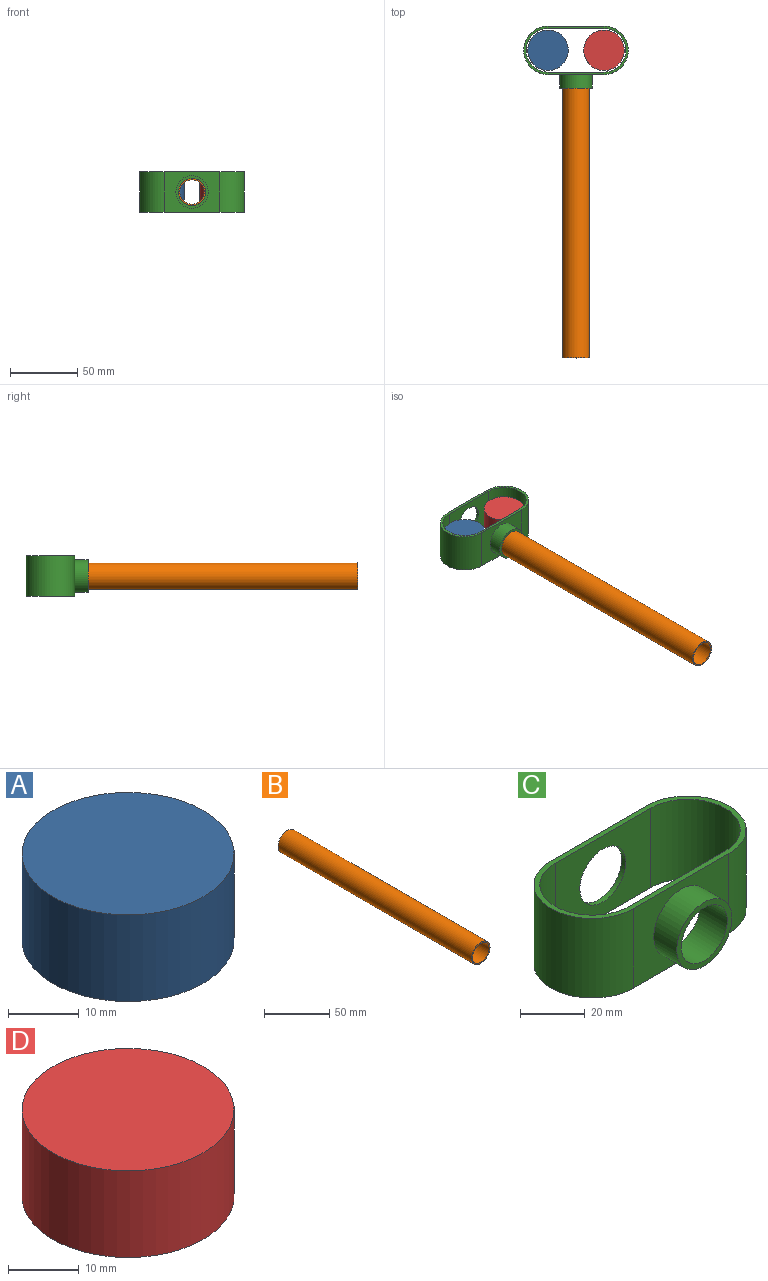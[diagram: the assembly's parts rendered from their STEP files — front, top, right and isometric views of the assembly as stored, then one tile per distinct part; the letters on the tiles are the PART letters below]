
ASSEMBLY  parts=4 mates=3
PART A: 3 faces, bbox 30x30x15 mm
  f0: cylinder r=15mm len=30mm, axis (0,0,-1), area 1413.7mm2, adj f1,f2
  f1: plane 30x30mm, normal (0,0,1), area 706.9mm2, adj f0
  f2: plane 30x30mm, normal (0,0,-1), area 706.9mm2, adj f0
PART B: 4 faces, bbox 20x210x20 mm
  f0: cylinder r=9mm len=210mm, axis (0,1,0), area 11875.2mm2, adj f2,f3
  f1: cylinder r=10mm len=210mm, axis (0,1,0), area 13194.7mm2, adj f2,f3
  f2: plane 20x20mm, normal (0,-1,0), area 59.7mm2, adj f0,f1
  f3: plane 20x20mm, normal (0,1,0), area 59.7mm2, adj f0,f1
PART C: 14 faces, bbox 77.5x46x30 mm
  f0: cylinder r=16.2mm len=32.4mm, axis (0,0,-1), area 1526.8mm2, adj f1,f7,f8,f9
  f1: plane 41.5x30mm, normal (0,-1,0), area 930.8mm2, adj f0,f2,f8,f9,f13
  f2: cylinder r=16.2mm len=32.4mm, axis (0,0,-1), area 1526.8mm2, adj f1,f7,f8,f9
  f3: plane 41.5x30mm, normal (0,1,0), area 930.8mm2, adj f4,f6,f8,f9,f13
  f4: cylinder r=18mm len=36mm, axis (0,0,-1), area 1696.5mm2, adj f3,f5,f8,f9
  f5: plane 41.5x30mm, normal (0,-1,0), area 792.6mm2, adj f4,f6,f8,f9,f11
  f6: cylinder r=18mm len=36mm, axis (0,0,-1), area 1696.5mm2, adj f3,f5,f8,f9
  f7: plane 41.5x30mm, normal (0,1,0), area 930.8mm2, adj f0,f2,f8,f9,f10
  f8: plane 77.5x36mm, normal (0,0,1), area 342.8mm2, adj f0,f1,f2,f3,f4,f5,f6,f7
  f9: plane 77.5x36mm, normal (0,0,-1), area 342.8mm2, adj f0,f1,f2,f3,f4,f5,f6,f7
  f10: cylinder r=10mm len=20mm, axis (0,1,0), area 741.4mm2, adj f7,f12
  f11: cylinder r=12mm len=24mm, axis (0,1,0), area 754mm2, adj f5,f12
  f12: plane 24x24mm, normal (0,-1,0), area 138.2mm2, adj f10,f11
  f13: cylinder r=10mm len=20mm, axis (0,-1,0), area 113.1mm2, adj f1,f3
PART D: 3 faces, bbox 30x30x15 mm
  f0: cylinder r=15mm len=30mm, axis (0,0,-1), area 1413.7mm2, adj f1,f2
  f1: plane 30x30mm, normal (0,0,1), area 706.9mm2, adj f0
  f2: plane 30x30mm, normal (0,0,-1), area 706.9mm2, adj f0
PLACE A t=(19.19,103.24,-27.5)mm
PLACE B rot(axis=(0,0,1),0deg) t=(9.37,85.24,9.93)mm
PLACE C rot(axis=(0,0,1),0deg) t=(11.79,1.65,-5.07)mm
PLACE D rot(axis=(0,0,1),0deg) t=(60.69,103.24,2.34)mm
MATE cylindrical D.f0 <-> C.f2  axis (0,0,-1) through (30.12,103.24,2.34)mm
MATE cylindrical A.f0 <-> C.f0  axis (0,0,-1) through (-11.38,103.24,10)mm
MATE fastened B.f1 <-> C.f10  axis (0,1,0) through (9.37,85.24,9.93)mm
